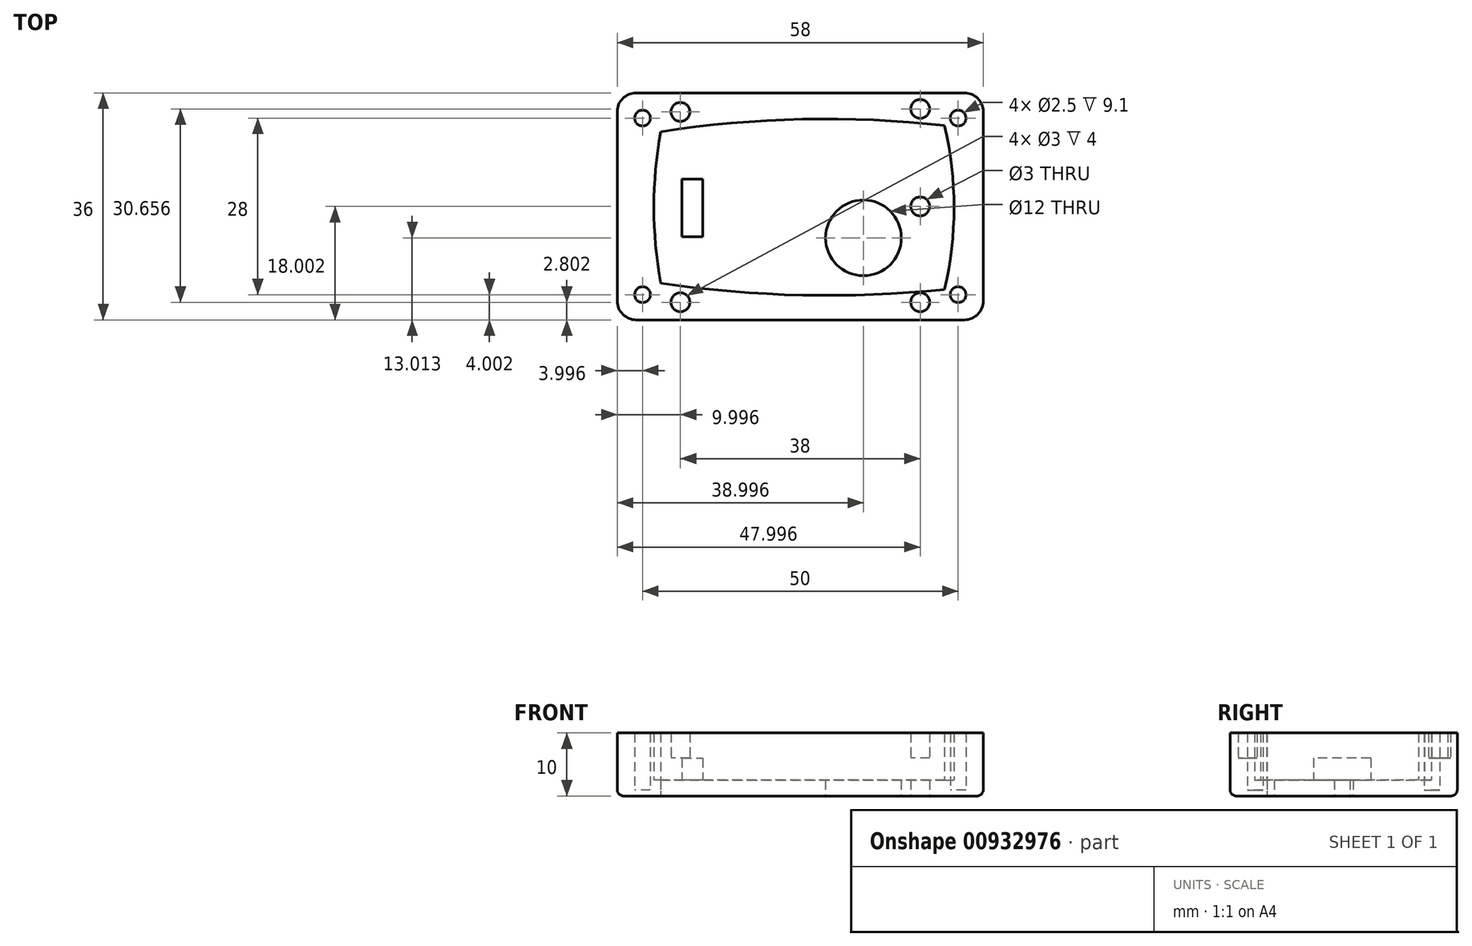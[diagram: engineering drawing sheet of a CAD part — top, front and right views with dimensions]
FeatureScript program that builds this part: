
annotation { "Feature Type Name" : "Feature", "Feature Type Description" : "" }
export const myFeature = defineFeature(function(context is Context, id is Id, definition is map)
    precondition{}
    {
        {
            var Q0;
            Q0=qCreatedBy(makeId("Top.planeOp"),FACE);
            var sketch = newSketch(context, id + "F0", { "sketchPlane" : qUnion([Q0])});
            skLineSegment(sketch, "E0", {"start": v(-0.01, 0.02) * mm, "end": v(-0.01, 24.02) * mm});
            skLineSegment(sketch, "E1", {"start": v(44.98, -1) * mm, "end": v(44.98, 25) * mm});
            skLineSegment(sketch, "E2", {"start": v(-0.01, 24.02) * mm, "end": v(44.98, 25) * mm});
            skLineSegment(sketch, "E3", {"start": v(-0.01, 0.02) * mm, "end": v(44.98, -1) * mm});
            skArc(sketch, "E4", {"start": v(44.98, 25) * mm, "mid": v(22.45, 26.01) * mm, "end": v(-0.01, 24.02) * mm});
            skArc(sketch, "E5", {"start": v(0, 0) * mm, "mid": v(22.46, -1.9) * mm, "end": v(44.98, -1) * mm});
            skArc(sketch, "E6", {"start": v(44.98, -1) * mm, "mid": v(46.47, 12) * mm, "end": v(44.98, 25) * mm});
            skArc(sketch, "E7", {"start": v(-0.01, 24.02) * mm, "mid": v(-1.07, 12.01) * mm, "end": v(0, 0) * mm});
            skCircle(sketch, "E8", {"center": v(2.96, 21.67) * mm, "radius": 1 * mm});
            skCircle(sketch, "E9", {"center": v(2.96, 2.08) * mm, "radius": 1 * mm});
            skCircle(sketch, "E10", {"center": v(41.71, 2.08) * mm, "radius": 1 * mm});
            skCircle(sketch, "E11", {"center": v(41.71, 21.67) * mm, "radius": 1 * mm});
            skLineSegment(sketch, "E12.bottom", {"start": v(-6.87, 30.18) * mm, "end": v(51.13, 30.18) * mm});
            skLineSegment(sketch, "E12.top", {"start": v(-6.87, -5.82) * mm, "end": v(51.13, -5.82) * mm});
            skLineSegment(sketch, "E12.left", {"start": v(-6.87, 30.18) * mm, "end": v(-6.87, -5.82) * mm});
            skLineSegment(sketch, "E12.right", {"start": v(51.13, 30.18) * mm, "end": v(51.13, -5.82) * mm});
            skCircle(sketch, "E13", {"center": v(-2.87, 26.18) * mm, "radius": 1.25 * mm});
            skCircle(sketch, "E14", {"center": v(-2.87, -1.82) * mm, "radius": 1.25 * mm});
            skCircle(sketch, "E15", {"center": v(47.13, 26.18) * mm, "radius": 1.25 * mm});
            skCircle(sketch, "E16", {"center": v(47.13, -1.82) * mm, "radius": 1.25 * mm});
            skCircle(sketch, "E17", {"center": v(18.8, 12.3) * mm, "radius": 1 * mm});
            skCircle(sketch, "E18", {"center": v(26.8, 12.3) * mm, "radius": 1 * mm});
            skLineSegment(sketch, "E19.bottom", {"start": v(3.37, 16.48) * mm, "end": v(6.66, 16.48) * mm});
            skLineSegment(sketch, "E19.top", {"start": v(3.37, 7.4) * mm, "end": v(6.66, 7.4) * mm});
            skLineSegment(sketch, "E19.left", {"start": v(3.37, 16.48) * mm, "end": v(3.37, 7.4) * mm});
            skLineSegment(sketch, "E19.right", {"start": v(6.66, 16.48) * mm, "end": v(6.66, 7.4) * mm});
            skLineSegment(sketch, "E20.bottom", {"start": v(26.13, 9.18) * mm, "end": v(38.13, 9.18) * mm});
            skLineSegment(sketch, "E20.top", {"start": v(26.13, 1.18) * mm, "end": v(38.13, 1.18) * mm});
            skLineSegment(sketch, "E20.left", {"start": v(26.13, 9.18) * mm, "end": v(26.13, 1.18) * mm});
            skLineSegment(sketch, "E20.right", {"start": v(38.13, 9.18) * mm, "end": v(38.13, 1.18) * mm});
            skCircle(sketch, "E21", {"center": v(32.13, 7.2) * mm, "radius": 6 * mm});
            skPoint(sketch, "E22", {"position": v(32.13, 9.18) * mm});
            skCircle(sketch, "E23", {"center": v(3.13, 27.16) * mm, "radius": 1.5 * mm});
            skCircle(sketch, "E24", {"center": v(41.13, 27.64) * mm, "radius": 1.5 * mm});
            skCircle(sketch, "E25", {"center": v(3.13, -3.02) * mm, "radius": 1.5 * mm});
            skCircle(sketch, "E26", {"center": v(41.13, -3.02) * mm, "radius": 1.5 * mm});
            skCircle(sketch, "E27", {"center": v(41.13, 12.18) * mm, "radius": 1.5 * mm});
            skSolve(sketch);
        }
        {
            var Q0;
            {var subQ1=sQuery(id+"F0.wireOp",EDGE,"E4");Q0=makeQuery(id+"F0.imprint","IMPRINT",FACE,{"disambiguationData":[TD([[makeQuery(id+"F0.imprint","IMPRINT",EDGE,{"derivedFrom":subQ1}),-1.0]])]});}
            var Q1;
            Q1=makeQuery(id+"F0.imprint","IMPRINT",FACE,{"disambiguationData":[TD([[makeQuery(id+"F0.imprint","IMPRINT",EDGE,{"derivedFrom":sQuery(id+"F0.wireOp",EDGE,"E13")}),1.0]])]});
            var Q2;
            Q2=makeQuery(id+"F0.imprint","IMPRINT",FACE,{"disambiguationData":[TD([[makeQuery(id+"F0.imprint","IMPRINT",EDGE,{"derivedFrom":sQuery(id+"F0.wireOp",EDGE,"E15")}),1.0]])]});
            var Q3;
            Q3=makeQuery(id+"F0.imprint","IMPRINT",FACE,{"disambiguationData":[TD([[makeQuery(id+"F0.imprint","IMPRINT",EDGE,{"derivedFrom":sQuery(id+"F0.wireOp",EDGE,"E16")}),1.0]])]});
            var Q4;
            Q4=makeQuery(id+"F0.imprint","IMPRINT",FACE,{"disambiguationData":[TD([[makeQuery(id+"F0.imprint","IMPRINT",EDGE,{"derivedFrom":sQuery(id+"F0.wireOp",EDGE,"E14")}),1.0]])]});
            var Q5;
            Q5=makeQuery(id+"F0.imprint","IMPRINT",FACE,{"disambiguationData":[TD([[makeQuery(id+"F0.imprint","IMPRINT",EDGE,{"derivedFrom":sQuery(id+"F0.wireOp",EDGE,"E25")}),1.0]])]});
            var Q6;
            Q6=makeQuery(id+"F0.imprint","IMPRINT",FACE,{"disambiguationData":[TD([[makeQuery(id+"F0.imprint","IMPRINT",EDGE,{"derivedFrom":sQuery(id+"F0.wireOp",EDGE,"E23")}),1.0]])]});
            var Q7;
            Q7=makeQuery(id+"F0.imprint","IMPRINT",FACE,{"disambiguationData":[TD([[makeQuery(id+"F0.imprint","IMPRINT",EDGE,{"derivedFrom":sQuery(id+"F0.wireOp",EDGE,"E24")}),1.0]])]});
            var Q8;
            Q8=makeQuery(id+"F0.imprint","IMPRINT",FACE,{"disambiguationData":[TD([[makeQuery(id+"F0.imprint","IMPRINT",EDGE,{"derivedFrom":sQuery(id+"F0.wireOp",EDGE,"E26")}),1.0]])]});
            extrude(context, id + "F1", {"entities" : qUnion([Q0, Q1, Q2, Q3, Q4, Q5, Q6, Q7, Q8]), "depth" : 10 * mm, "offsetDistance" : 25 * mm});
        }
        {
            var Q0;
            {var subQ1=sQuery(id+"F0.wireOp",EDGE,"E1");Q0=makeQuery(id+"F0.imprint","IMPRINT",FACE,{"disambiguationData":[TD([[makeQuery(id+"F0.imprint","IMPRINT",EDGE,{"derivedFrom":subQ1}),1.0]])]});}
            var Q1;
            Q1=makeQuery(id+"F0.imprint","IMPRINT",FACE,{"disambiguationData":[TD([[makeQuery(id+"F0.imprint","IMPRINT",EDGE,{"derivedFrom":sQuery(id+"F0.wireOp",EDGE,"E8")}),1.0]])]});
            var Q2;
            Q2=makeQuery(id+"F0.imprint","IMPRINT",FACE,{"disambiguationData":[TD([[makeQuery(id+"F0.imprint","IMPRINT",EDGE,{"derivedFrom":sQuery(id+"F0.wireOp",EDGE,"E9")}),1.0]])]});
            var Q3;
            Q3=makeQuery(id+"F0.imprint","IMPRINT",FACE,{"disambiguationData":[TD([[makeQuery(id+"F0.imprint","IMPRINT",EDGE,{"derivedFrom":sQuery(id+"F0.wireOp",EDGE,"E10")}),1.0]])]});
            var Q4;
            Q4=makeQuery(id+"F0.imprint","IMPRINT",FACE,{"disambiguationData":[TD([[makeQuery(id+"F0.imprint","IMPRINT",EDGE,{"derivedFrom":sQuery(id+"F0.wireOp",EDGE,"E11")}),1.0]])]});
            var Q5;
            Q5=makeQuery(id+"F0.imprint","IMPRINT",FACE,{"disambiguationData":[TD([[makeQuery(id+"F0.imprint","IMPRINT",EDGE,{"derivedFrom":sQuery(id+"F0.wireOp",EDGE,"E2")}),1.0]])]});
            var Q6;
            {var subQ0=sQuery(id+"F0.wireOp",EDGE,"E5");Q6=makeQuery(id+"F0.imprint","IMPRINT",FACE,{"disambiguationData":[TD([[makeQuery(id+"F0.imprint","IMPRINT",EDGE,{"derivedFrom":subQ0}),1.0]])]});}
            var Q7;
            Q7=makeQuery(id+"F0.imprint","IMPRINT",FACE,{"disambiguationData":[TD([[makeQuery(id+"F0.imprint","IMPRINT",EDGE,{"derivedFrom":sQuery(id+"F0.wireOp",EDGE,"E1")}),-1.0]])]});
            var Q8;
            {var subQ0=sQuery(id+"F0.wireOp",EDGE,"E7");var subQ1=sQuery(id+"F0.wireOp",EDGE,"E0");var subQ3=makeQuery(id+"F0.imprint","INTERSECT",VERTEX,{"derivedFrom":[subQ1,subQ0]});Q8=makeQuery(id+"F0.imprint","IMPRINT",FACE,{"disambiguationData":[TD([[makeQuery(id+"F0.imprint","IMPRINT",EDGE,{"disambiguationData":[TD([[subQ3,-1.0]])],"derivedFrom":subQ1}),1.0]])]});}
            var Q9;
            Q9=makeQuery(id+"F0.imprint","IMPRINT",FACE,{"disambiguationData":[TD([[makeQuery(id+"F0.imprint","IMPRINT",EDGE,{"derivedFrom":sQuery(id+"F0.wireOp",EDGE,"E19.bottom")}),-1.0]])]});
            var Q10;
            Q10=makeQuery(id+"F0.imprint","IMPRINT",FACE,{"disambiguationData":[TD([[makeQuery(id+"F0.imprint","IMPRINT",EDGE,{"derivedFrom":sQuery(id+"F0.wireOp",EDGE,"E17")}),1.0]])]});
            var Q11;
            Q11=makeQuery(id+"F0.imprint","IMPRINT",FACE,{"disambiguationData":[TD([[makeQuery(id+"F0.imprint","IMPRINT",EDGE,{"derivedFrom":sQuery(id+"F0.wireOp",EDGE,"E18")}),1.0]])]});
            var Q12;
            Q12=makeQuery(id+"F0.imprint","IMPRINT",FACE,{"disambiguationData":[TD([[makeQuery(id+"F0.imprint","IMPRINT",EDGE,{"derivedFrom":sQuery(id+"F0.wireOp",EDGE,"E20.bottom")}),-1.0]])]});
            var Q13;
            {var subQ0=sQuery(id+"F0.wireOp",EDGE,"E20.right");var subQ1=sQuery(id+"F0.wireOp",EDGE,"E20.top");var subQ2=makeQuery(id+"F0.imprint","INTERSECT",VERTEX,{"derivedFrom":[subQ1,subQ0]});Q13=makeQuery(id+"F0.imprint","IMPRINT",FACE,{"disambiguationData":[TD([[makeQuery(id+"F0.imprint","IMPRINT",EDGE,{"disambiguationData":[TD([[subQ2,1.0]])],"derivedFrom":subQ1}),1.0]])]});}
            extrude(context, id + "F2", {"entities" : qUnion([Q0, Q1, Q2, Q3, Q4, Q5, Q6, Q7, Q8, Q9, Q10, Q11, Q12, Q13]), "operationType" : NewBodyOperationType.ADD, "depth" : 2.5 * mm, "offsetDistance" : 25 * mm});
        }
        {
            var Q0;
            Q0=makeQuery(id+"F1.opExtrude","SWEPT_EDGE",EDGE,{"disambiguationData":[OSD([sQuery(id+"F0.wireOp",EDGE,"E12.bottom"),sQuery(id+"F0.wireOp",EDGE,"E12.right")])]});
            var Q1;
            Q1=makeQuery(id+"F1.opExtrude","SWEPT_EDGE",EDGE,{"disambiguationData":[OSD([sQuery(id+"F0.wireOp",EDGE,"E12.top"),sQuery(id+"F0.wireOp",EDGE,"E12.right")])]});
            var Q2;
            Q2=makeQuery(id+"F1.opExtrude","SWEPT_EDGE",EDGE,{"disambiguationData":[OSD([sQuery(id+"F0.wireOp",EDGE,"E12.top"),sQuery(id+"F0.wireOp",EDGE,"E12.left")])]});
            var Q3;
            Q3=makeQuery(id+"F1.opExtrude","SWEPT_EDGE",EDGE,{"disambiguationData":[OSD([sQuery(id+"F0.wireOp",EDGE,"E12.bottom"),sQuery(id+"F0.wireOp",EDGE,"E12.left")])]});
            fillet(context, id + "F3", {"entities" : qUnion([Q0, Q1, Q2, Q3]), "radius" : 3 * mm, "tangentPropagation" : true, "allowEdgeOverflow" : false});
        }
        {
            var Q0;
            Q0=makeQuery(id+"F0.imprint","IMPRINT",FACE,{"disambiguationData":[TD([[makeQuery(id+"F0.imprint","IMPRINT",EDGE,{"derivedFrom":sQuery(id+"F0.wireOp",EDGE,"E19.bottom")}),-1.0]])]});
            extrude(context, id + "F4", {"entities" : qUnion([Q0]), "operationType" : NewBodyOperationType.ADD, "depth" : 6 * mm, "offsetDistance" : 25 * mm});
        }
        {
            var Q0;
            Q0=makeQuery(id+"F0.imprint","IMPRINT",FACE,{"disambiguationData":[TD([[makeQuery(id+"F0.imprint","IMPRINT",EDGE,{"derivedFrom":sQuery(id+"F0.wireOp",EDGE,"E15")}),1.0]])]});
            var Q1;
            Q1=makeQuery(id+"F0.imprint","IMPRINT",FACE,{"disambiguationData":[TD([[makeQuery(id+"F0.imprint","IMPRINT",EDGE,{"derivedFrom":sQuery(id+"F0.wireOp",EDGE,"E13")}),1.0]])]});
            var Q2;
            Q2=makeQuery(id+"F0.imprint","IMPRINT",FACE,{"disambiguationData":[TD([[makeQuery(id+"F0.imprint","IMPRINT",EDGE,{"derivedFrom":sQuery(id+"F0.wireOp",EDGE,"E14")}),1.0]])]});
            var Q3;
            Q3=makeQuery(id+"F0.imprint","IMPRINT",FACE,{"disambiguationData":[TD([[makeQuery(id+"F0.imprint","IMPRINT",EDGE,{"derivedFrom":sQuery(id+"F0.wireOp",EDGE,"E16")}),1.0]])]});
            extrude(context, id + "F5", {"entities" : qUnion([Q0, Q1, Q2, Q3]), "operationType" : NewBodyOperationType.REMOVE, "depth" : 17.1 * mm, "offsetDistance" : 25 * mm, "hasSecondDirection" : true, "secondDirectionOppositeDirection" : false, "secondDirectionDepth" : 0.9 * mm});
        }
        {
            var Q0;
            Q0=makeQuery(id+"F0.imprint","IMPRINT",FACE,{"disambiguationData":[TD([[makeQuery(id+"F0.imprint","IMPRINT",EDGE,{"derivedFrom":sQuery(id+"F0.wireOp",EDGE,"E23")}),1.0]])]});
            var Q1;
            Q1=makeQuery(id+"F0.imprint","IMPRINT",FACE,{"disambiguationData":[TD([[makeQuery(id+"F0.imprint","IMPRINT",EDGE,{"derivedFrom":sQuery(id+"F0.wireOp",EDGE,"E24")}),1.0]])]});
            var Q2;
            Q2=makeQuery(id+"F0.imprint","IMPRINT",FACE,{"disambiguationData":[TD([[makeQuery(id+"F0.imprint","IMPRINT",EDGE,{"derivedFrom":sQuery(id+"F0.wireOp",EDGE,"E26")}),1.0]])]});
            var Q3;
            Q3=makeQuery(id+"F0.imprint","IMPRINT",FACE,{"disambiguationData":[TD([[makeQuery(id+"F0.imprint","IMPRINT",EDGE,{"derivedFrom":sQuery(id+"F0.wireOp",EDGE,"E25")}),1.0]])]});
            extrude(context, id + "F6", {"entities" : qUnion([Q0, Q1, Q2, Q3]), "operationType" : NewBodyOperationType.REMOVE, "depth" : 16.7 * mm, "offsetDistance" : 25 * mm, "hasSecondDirection" : true, "secondDirectionOppositeDirection" : false, "secondDirectionDepth" : 6 * mm});
        }
        {
            var Q0;
            Q0=makeQuery(id+"F1.opExtrude","CAP_EDGE",EDGE,{"disambiguationData":[OSD([sQuery(id+"F0.wireOp",EDGE,"E12.right")])],"isStart":true});
            fillet(context, id + "F7", {"entities" : qUnion([Q0]), "radius" : 1 * mm, "tangentPropagation" : true, "allowEdgeOverflow" : false});
        }
    });
